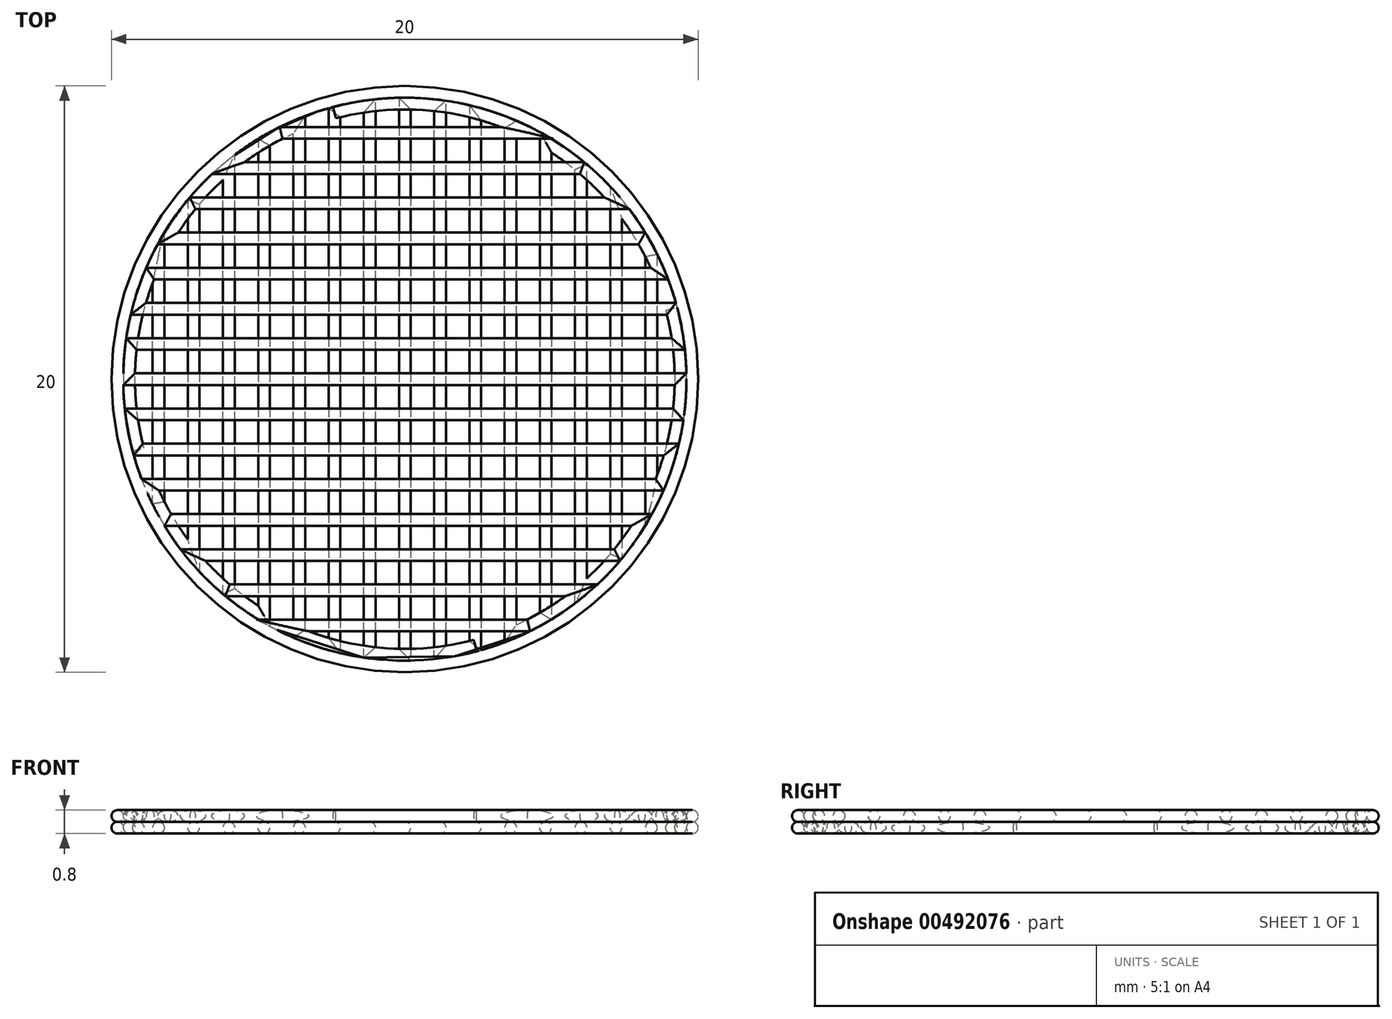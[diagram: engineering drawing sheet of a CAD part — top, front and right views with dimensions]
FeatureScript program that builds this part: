
annotation { "Feature Type Name" : "Feature", "Feature Type Description" : "" }
export const myFeature = defineFeature(function(context is Context, id is Id, definition is map)
    precondition{}
    {
        {
            assignVariable(context, id + "F0", {"name" : "d", "anyValue" : 0.4 * mm});
        }
        {
            var Q0;
            Q0=qCreatedBy(makeId("Top.planeOp"),FACE);
            cPlane(context, id + "F1", {"entities" : qUnion([Q0]), "cplaneType" : CPlaneType.OFFSET, "offset" : getVariable(context, 'd') / 2, "width" : 150 * mm, "height" : 150 * mm});
        }
        {
            var Q0;
            Q0=qCreatedBy(id+"F1.planeOp",FACE);
            var sketch = newSketch(context, id + "F2", { "sketchPlane" : qUnion([Q0])});
            skLineSegment(sketch, "E0.bottom", {"start": v(10, 10) * mm, "end": v(-10, 10) * mm, "construction": true});
            skLineSegment(sketch, "E0.top", {"start": v(10, -10) * mm, "end": v(-10, -10) * mm, "construction": true});
            skLineSegment(sketch, "E0.left", {"start": v(10, 10) * mm, "end": v(10, -10) * mm, "construction": true});
            skLineSegment(sketch, "E0.right", {"start": v(-10, 10) * mm, "end": v(-10, -10) * mm, "construction": true});
            skPoint(sketch, "E0.middle", {"position": v(0, 0) * mm});
            skCircle(sketch, "E1", {"center": v(0, 0) * mm, "radius": 9.8 * mm});
            skCircle(sketch, "E2", {"center": v(0, 0) * mm, "radius": 9.4 * mm, "construction": true});
            skLineSegment(sketch, "E3", {"start": v(10, -10) * mm, "end": v(9.6, -10) * mm, "construction": true});
            skLineSegment(sketch, "E4", {"start": v(9.6, -10) * mm, "end": v(8.4, -10) * mm, "construction": true});
            skLineSegment(sketch, "E5", {"start": v(8.4, -10) * mm, "end": v(7.2, -10) * mm, "construction": true});
            skLineSegment(sketch, "E6", {"start": v(7.2, -10) * mm, "end": v(6, -10) * mm, "construction": true});
            skLineSegment(sketch, "E7", {"start": v(6, -10) * mm, "end": v(4.8, -10) * mm, "construction": true});
            skLineSegment(sketch, "E8", {"start": v(4.8, -10) * mm, "end": v(3.6, -10) * mm, "construction": true});
            skLineSegment(sketch, "E9", {"start": v(3.6, -10) * mm, "end": v(2.4, -10) * mm, "construction": true});
            skLineSegment(sketch, "E10", {"start": v(2.4, -10) * mm, "end": v(1.2, -10) * mm, "construction": true});
            skLineSegment(sketch, "E11", {"start": v(1.2, -10) * mm, "end": v(0, -10) * mm, "construction": true});
            skLineSegment(sketch, "E12", {"start": v(0, -10) * mm, "end": v(-1.2, -10) * mm, "construction": true});
            skLineSegment(sketch, "E13", {"start": v(-1.2, -10) * mm, "end": v(-2.4, -10) * mm, "construction": true});
            skLineSegment(sketch, "E14", {"start": v(-2.4, -10) * mm, "end": v(-3.6, -10) * mm, "construction": true});
            skLineSegment(sketch, "E15", {"start": v(-3.6, -10) * mm, "end": v(-4.8, -10) * mm, "construction": true});
            skLineSegment(sketch, "E16", {"start": v(-4.8, -10) * mm, "end": v(-6, -10) * mm, "construction": true});
            skLineSegment(sketch, "E17", {"start": v(-6, -10) * mm, "end": v(-10, -10) * mm, "construction": true});
            skLineSegment(sketch, "E18", {"start": v(-6, -10) * mm, "end": v(-7.2, -10) * mm, "construction": true});
            skLineSegment(sketch, "E19", {"start": v(-7.2, -10) * mm, "end": v(-8.4, -10) * mm, "construction": true});
            skLineSegment(sketch, "E20", {"start": v(-8.4, -10) * mm, "end": v(-9.6, -10) * mm, "construction": true});
            skLineSegment(sketch, "E21", {"start": v(-9.6, -10) * mm, "end": v(-10, -10) * mm, "construction": true});
            skLineSegment(sketch, "E22", {"start": v(9.6, -10) * mm, "end": v(9.6, 10) * mm, "construction": true});
            skLineSegment(sketch, "E23", {"start": v(9.6, 10) * mm, "end": v(10, 10) * mm, "construction": true});
            skLineSegment(sketch, "E24", {"start": v(-9.6, -10) * mm, "end": v(-9.6, 10) * mm, "construction": true});
            skLineSegment(sketch, "E25", {"start": v(-9.6, 10) * mm, "end": v(-10, 10) * mm, "construction": true});
            skLineSegment(sketch, "E26", {"start": v(7.2, -10) * mm, "end": v(7.2, -6.04) * mm, "construction": true});
            skLineSegment(sketch, "E27", {"start": v(7.2, -6.04) * mm, "end": v(7.2, 6.04) * mm});
            skLineSegment(sketch, "E28", {"start": v(7.2, 6.04) * mm, "end": v(7.2, 10) * mm, "construction": true});
            skLineSegment(sketch, "E29", {"start": v(6, -10) * mm, "end": v(6, -7.24) * mm, "construction": true});
            skLineSegment(sketch, "E30", {"start": v(6, -7.24) * mm, "end": v(6, 7.24) * mm});
            skLineSegment(sketch, "E31", {"start": v(6, 7.24) * mm, "end": v(6, 10) * mm, "construction": true});
            skLineSegment(sketch, "E32", {"start": v(6, 10) * mm, "end": v(7.2, 10) * mm, "construction": true});
            skLineSegment(sketch, "E33", {"start": v(4.8, -10) * mm, "end": v(4.8, -8.08) * mm, "construction": true});
            skLineSegment(sketch, "E34", {"start": v(4.8, -8.08) * mm, "end": v(4.8, 8.08) * mm});
            skLineSegment(sketch, "E35", {"start": v(4.8, 8.08) * mm, "end": v(4.8, 10) * mm, "construction": true});
            skLineSegment(sketch, "E36", {"start": v(4.8, 10) * mm, "end": v(6, 10) * mm, "construction": true});
            skLineSegment(sketch, "E37", {"start": v(3.6, -10) * mm, "end": v(3.6, -8.68) * mm, "construction": true});
            skLineSegment(sketch, "E38", {"start": v(3.6, -8.68) * mm, "end": v(3.6, 8.68) * mm});
            skLineSegment(sketch, "E39", {"start": v(3.6, 8.68) * mm, "end": v(3.6, 10) * mm, "construction": true});
            skLineSegment(sketch, "E40", {"start": v(3.6, 10) * mm, "end": v(4.8, 10) * mm, "construction": true});
            skLineSegment(sketch, "E41", {"start": v(2.4, -10) * mm, "end": v(2.4, -9.09) * mm, "construction": true});
            skLineSegment(sketch, "E42", {"start": v(2.4, -9.09) * mm, "end": v(2.4, 9.09) * mm});
            skLineSegment(sketch, "E43", {"start": v(2.4, 9.09) * mm, "end": v(2.4, 10) * mm, "construction": true});
            skLineSegment(sketch, "E44", {"start": v(2.4, 10) * mm, "end": v(3.6, 10) * mm, "construction": true});
            skLineSegment(sketch, "E45", {"start": v(1.2, -10) * mm, "end": v(1.2, -9.32) * mm, "construction": true});
            skLineSegment(sketch, "E46", {"start": v(1.2, -9.32) * mm, "end": v(1.2, 9.32) * mm});
            skLineSegment(sketch, "E47", {"start": v(1.2, 9.32) * mm, "end": v(1.2, 10) * mm, "construction": true});
            skLineSegment(sketch, "E48", {"start": v(1.2, 10) * mm, "end": v(2.4, 10) * mm, "construction": true});
            skLineSegment(sketch, "E49", {"start": v(0, -10) * mm, "end": v(0, -9.4) * mm, "construction": true});
            skLineSegment(sketch, "E50", {"start": v(0, -9.4) * mm, "end": v(0, 9.4) * mm});
            skLineSegment(sketch, "E51", {"start": v(0, 9.4) * mm, "end": v(0, 10) * mm, "construction": true});
            skLineSegment(sketch, "E52", {"start": v(0, 10) * mm, "end": v(1.2, 10) * mm, "construction": true});
            skLineSegment(sketch, "E53", {"start": v(-1.2, -10) * mm, "end": v(-1.2, -9.32) * mm, "construction": true});
            skLineSegment(sketch, "E54", {"start": v(-1.2, -9.32) * mm, "end": v(-1.2, 9.32) * mm});
            skLineSegment(sketch, "E55", {"start": v(-1.2, 9.32) * mm, "end": v(-1.2, 10) * mm, "construction": true});
            skLineSegment(sketch, "E56", {"start": v(-1.2, 10) * mm, "end": v(0, 10) * mm, "construction": true});
            skLineSegment(sketch, "E57", {"start": v(-2.4, -10) * mm, "end": v(-2.4, -9.09) * mm, "construction": true});
            skLineSegment(sketch, "E58", {"start": v(-2.4, -9.09) * mm, "end": v(-2.4, 9.09) * mm});
            skLineSegment(sketch, "E59", {"start": v(-2.4, 9.09) * mm, "end": v(-2.4, 10) * mm, "construction": true});
            skLineSegment(sketch, "E60", {"start": v(-2.4, 10) * mm, "end": v(-1.2, 10) * mm, "construction": true});
            skLineSegment(sketch, "E61", {"start": v(-3.6, -10) * mm, "end": v(-3.6, -8.68) * mm, "construction": true});
            skLineSegment(sketch, "E62", {"start": v(-3.6, -8.68) * mm, "end": v(-3.6, 8.68) * mm});
            skLineSegment(sketch, "E63", {"start": v(-3.6, 8.68) * mm, "end": v(-3.6, 10) * mm, "construction": true});
            skLineSegment(sketch, "E64", {"start": v(-3.6, 10) * mm, "end": v(-2.4, 10) * mm, "construction": true});
            skLineSegment(sketch, "E65", {"start": v(-4.8, -10) * mm, "end": v(-4.8, -8.08) * mm, "construction": true});
            skLineSegment(sketch, "E66", {"start": v(-4.8, -8.08) * mm, "end": v(-4.8, 8.08) * mm});
            skLineSegment(sketch, "E67", {"start": v(-4.8, 8.08) * mm, "end": v(-4.8, 10) * mm, "construction": true});
            skLineSegment(sketch, "E68", {"start": v(-4.8, 10) * mm, "end": v(-3.6, 10) * mm, "construction": true});
            skLineSegment(sketch, "E69", {"start": v(-6, -10) * mm, "end": v(-6, -7.24) * mm, "construction": true});
            skLineSegment(sketch, "E70", {"start": v(-6, -7.24) * mm, "end": v(-6, 7.24) * mm});
            skLineSegment(sketch, "E71", {"start": v(-6, 7.24) * mm, "end": v(-6, 10) * mm, "construction": true});
            skLineSegment(sketch, "E72", {"start": v(-6, 10) * mm, "end": v(-4.8, 10) * mm, "construction": true});
            skLineSegment(sketch, "E73", {"start": v(-7.2, -10) * mm, "end": v(-7.2, -6.04) * mm, "construction": true});
            skLineSegment(sketch, "E74", {"start": v(-7.2, -6.04) * mm, "end": v(-7.2, 6.04) * mm});
            skLineSegment(sketch, "E75", {"start": v(-7.2, 6.04) * mm, "end": v(-7.2, 10) * mm, "construction": true});
            skLineSegment(sketch, "E76", {"start": v(-7.2, 10) * mm, "end": v(-6, 10) * mm, "construction": true});
            skLineSegment(sketch, "E77", {"start": v(-8.4, -10) * mm, "end": v(-8.4, -4.22) * mm, "construction": true});
            skArc(sketch, "E78", {"start": v(6, 7.24) * mm, "mid": v(5.42, 7.68) * mm, "end": v(4.8, 8.08) * mm});
            skArc(sketch, "E79", {"start": v(3.6, 8.68) * mm, "mid": v(3, 8.9) * mm, "end": v(2.4, 9.09) * mm});
            skArc(sketch, "E80", {"start": v(1.2, 9.32) * mm, "mid": v(0.6, 9.38) * mm, "end": v(0, 9.4) * mm});
            skArc(sketch, "E81", {"start": v(-1.2, 9.32) * mm, "mid": v(-1.8, 9.23) * mm, "end": v(-2.4, 9.09) * mm});
            skArc(sketch, "E82", {"start": v(-3.6, 8.68) * mm, "mid": v(-4.21, 8.4) * mm, "end": v(-4.8, 8.08) * mm});
            skArc(sketch, "E83", {"start": v(-6, 7.24) * mm, "mid": v(-6.63, 6.67) * mm, "end": v(-7.2, 6.04) * mm});
            skArc(sketch, "E84", {"start": v(7.2, -6.04) * mm, "mid": v(6.63, -6.67) * mm, "end": v(6, -7.24) * mm});
            skArc(sketch, "E85", {"start": v(4.8, -8.08) * mm, "mid": v(4.21, -8.4) * mm, "end": v(3.6, -8.68) * mm});
            skArc(sketch, "E86", {"start": v(2.4, -9.09) * mm, "mid": v(1.8, -9.23) * mm, "end": v(1.2, -9.32) * mm});
            skArc(sketch, "E87", {"start": v(0, -9.4) * mm, "mid": v(-0.6, -9.38) * mm, "end": v(-1.2, -9.32) * mm});
            skArc(sketch, "E88", {"start": v(-2.4, -9.09) * mm, "mid": v(-3, -8.9) * mm, "end": v(-3.6, -8.68) * mm});
            skArc(sketch, "E89", {"start": v(-4.8, -8.08) * mm, "mid": v(-5.42, -7.68) * mm, "end": v(-6, -7.24) * mm});
            skArc(sketch, "E90", {"start": v(-7.2, -6.04) * mm, "mid": v(-7.85, -5.17) * mm, "end": v(-8.4, -4.22) * mm});
            skLineSegment(sketch, "E91", {"start": v(8.4, -10) * mm, "end": v(8.4, -5.05) * mm, "construction": true});
            skLineSegment(sketch, "E92", {"start": v(8.4, -5.05) * mm, "end": v(8.4, 4.22) * mm});
            skLineSegment(sketch, "E93", {"start": v(8.4, 4.22) * mm, "end": v(8.4, 10) * mm, "construction": true});
            skLineSegment(sketch, "E94", {"start": v(8.4, 10) * mm, "end": v(9.6, 10) * mm, "construction": true});
            skLineSegment(sketch, "E95", {"start": v(7.2, 10) * mm, "end": v(8.4, 10) * mm, "construction": true});
            skLineSegment(sketch, "E96", {"start": v(-8.4, -4.22) * mm, "end": v(-8.4, 5.05) * mm});
            skLineSegment(sketch, "E97", {"start": v(-8.4, 5.05) * mm, "end": v(-8.4, 10) * mm, "construction": true});
            skLineSegment(sketch, "E98", {"start": v(-8.4, 10) * mm, "end": v(-7.2, 10) * mm, "construction": true});
            skLineSegment(sketch, "E99", {"start": v(-8.4, 10) * mm, "end": v(-9.6, 10) * mm, "construction": true});
            skArc(sketch, "E100", {"start": v(8.4, 4.22) * mm, "mid": v(7.85, 5.17) * mm, "end": v(7.2, 6.04) * mm});
            skLineSegment(sketch, "E101", {"start": v(-8.4, -4.22) * mm, "end": v(-8.4, 4.22) * mm});
            skLineSegment(sketch, "E102", {"start": v(8.4, -4.22) * mm, "end": v(8.4, 4.22) * mm});
            skPoint(sketch, "E103", {"position": v(9.09, 10) * mm});
            skPoint(sketch, "E104", {"position": v(9.09, 2.4) * mm});
            skArc(sketch, "E105", {"start": v(8.4, -4.22) * mm, "mid": v(9.35, -0.97) * mm, "end": v(9.09, 2.4) * mm});
            skPoint(sketch, "E106", {"position": v(-9.09, -10) * mm});
            skPoint(sketch, "E107", {"position": v(-9.09, -2.4) * mm});
            skArc(sketch, "E108", {"start": v(-8.4, 4.22) * mm, "mid": v(-9.35, 0.97) * mm, "end": v(-9.09, -2.4) * mm});
            skSolve(sketch);
        }
        {
            var Q0;
            Q0=sQuery(id+"F2.wireOp",EDGE,"E105");
            var Q1;
            Q1=sQuery(id+"F2.wireOp",VERTEX,"E104");
            cPlane(context, id + "F3", {"entities" : qUnion([Q0, Q1]), "cplaneType" : CPlaneType.CURVE_POINT, "offset" : 25 * mm, "width" : 150 * mm, "height" : 150 * mm});
        }
        {
            var Q0;
            Q0=qCreatedBy(id+"F3.planeOp",FACE);
            var sketch = newSketch(context, id + "F4", { "sketchPlane" : qUnion([Q0])});
            skCircle(sketch, "E109", {"center": v(-9.4, 0.2) * mm, "radius": 0.2 * mm});
            skSolve(sketch);
        }
        {
            var Q0;
            Q0=makeQuery(id+"F4.imprint","IMPRINT",FACE,{"disambiguationData":[TD([[makeQuery(id+"F4.imprint","IMPRINT",EDGE,{"derivedFrom":sQuery(id+"F4.wireOp",EDGE,"E109")}),1.0]])]});
            var Q1;
            Q1=sQuery(id+"F2.wireOp",EDGE,"E105");
            var Q2;
            Q2=sQuery(id+"F2.wireOp",EDGE,"E102");
            var Q3;
            Q3=sQuery(id+"F2.wireOp",EDGE,"E100");
            var Q4;
            Q4=sQuery(id+"F2.wireOp",EDGE,"E27");
            var Q5;
            Q5=sQuery(id+"F2.wireOp",EDGE,"E84");
            var Q6;
            Q6=sQuery(id+"F2.wireOp",EDGE,"E30");
            var Q7;
            Q7=sQuery(id+"F2.wireOp",EDGE,"E78");
            var Q8;
            Q8=sQuery(id+"F2.wireOp",EDGE,"E34");
            var Q9;
            Q9=sQuery(id+"F2.wireOp",EDGE,"E85");
            var Q10;
            Q10=sQuery(id+"F2.wireOp",EDGE,"E38");
            var Q11;
            Q11=sQuery(id+"F2.wireOp",EDGE,"E79");
            var Q12;
            Q12=sQuery(id+"F2.wireOp",EDGE,"E42");
            var Q13;
            Q13=sQuery(id+"F2.wireOp",EDGE,"E86");
            var Q14;
            Q14=sQuery(id+"F2.wireOp",EDGE,"E46");
            var Q15;
            Q15=sQuery(id+"F2.wireOp",EDGE,"E50");
            var Q16;
            Q16=sQuery(id+"F2.wireOp",EDGE,"E80");
            var Q17;
            Q17=sQuery(id+"F2.wireOp",EDGE,"E81");
            var Q18;
            Q18=sQuery(id+"F2.wireOp",EDGE,"E54");
            var Q19;
            Q19=sQuery(id+"F2.wireOp",EDGE,"E58");
            var Q20;
            Q20=sQuery(id+"F2.wireOp",EDGE,"E82");
            var Q21;
            Q21=sQuery(id+"F2.wireOp",EDGE,"E62");
            var Q22;
            Q22=sQuery(id+"F2.wireOp",EDGE,"E66");
            var Q23;
            Q23=sQuery(id+"F2.wireOp",EDGE,"E70");
            var Q24;
            Q24=sQuery(id+"F2.wireOp",EDGE,"E83");
            var Q25;
            Q25=sQuery(id+"F2.wireOp",EDGE,"E74");
            var Q26;
            Q26=sQuery(id+"F2.wireOp",EDGE,"E101");
            var Q27;
            Q27=sQuery(id+"F2.wireOp",EDGE,"E90");
            var Q28;
            Q28=sQuery(id+"F2.wireOp",EDGE,"E89");
            var Q29;
            Q29=sQuery(id+"F2.wireOp",EDGE,"E88");
            var Q30;
            Q30=sQuery(id+"F2.wireOp",EDGE,"E87");
            var Q31;
            Q31=sQuery(id+"F2.wireOp",EDGE,"E108");
            sweep(context, id + "F5", {"profiles" : qUnion([Q0]), "path" : qUnion([Q1, Q2, Q3, Q4, Q5, Q6, Q7, Q8, Q9, Q10, Q11, Q12, Q13, Q14, Q15, Q16, Q17, Q18, Q19, Q20, Q21, Q22, Q23, Q24, Q25, Q26, Q27, Q28, Q29, Q30, Q31])});
        }
        {
            var Q0;
            Q0=qCreatedBy(makeId("Front.planeOp"),FACE);
            var sketch = newSketch(context, id + "F6", { "sketchPlane" : qUnion([Q0])});
            skCircle(sketch, "E110", {"center": v(9.8, 0.2) * mm, "radius": 0.2 * mm});
            skSolve(sketch);
        }
        {
            var Q0;
            Q0=qSketchRegion(id+"F6",true);
            var Q1;
            Q1=sQuery(id+"F2.wireOp",EDGE,"E1");
            sweep(context, id + "F7", {"profiles" : qUnion([Q0]), "path" : qUnion([Q1])});
        }
        {
            var Q0;
            Q0=qCreatedBy(id+"F1.planeOp",FACE);
            cPlane(context, id + "F8", {"entities" : qUnion([Q0]), "cplaneType" : CPlaneType.OFFSET, "offset" : getVariable(context, 'd'), "width" : 150 * mm, "height" : 150 * mm});
        }
        {
            var Q0;
            Q0=qCreatedBy(id+"F8.planeOp",FACE);
            var sketch = newSketch(context, id + "F9", { "sketchPlane" : qUnion([Q0])});
            skLineSegment(sketch, "E111.bottom", {"start": v(-10, 10) * mm, "end": v(-10, -10) * mm, "construction": true});
            skLineSegment(sketch, "E111.top", {"start": v(10, 10) * mm, "end": v(10, -10) * mm, "construction": true});
            skLineSegment(sketch, "E111.left", {"start": v(-10, 10) * mm, "end": v(10, 10) * mm, "construction": true});
            skLineSegment(sketch, "E111.right", {"start": v(-10, -10) * mm, "end": v(10, -10) * mm, "construction": true});
            skPoint(sketch, "E111.middle", {"position": v(0, 0) * mm});
            skCircle(sketch, "E112", {"center": v(0, 0) * mm, "radius": 9.8 * mm});
            skCircle(sketch, "E113", {"center": v(0, 0) * mm, "radius": 9.4 * mm, "construction": true});
            skLineSegment(sketch, "E114", {"start": v(10, 10) * mm, "end": v(10, 9.6) * mm, "construction": true});
            skLineSegment(sketch, "E115", {"start": v(10, 9.6) * mm, "end": v(10, 8.4) * mm, "construction": true});
            skLineSegment(sketch, "E116", {"start": v(10, 8.4) * mm, "end": v(10, 7.2) * mm, "construction": true});
            skLineSegment(sketch, "E117", {"start": v(10, 7.2) * mm, "end": v(10, 6) * mm, "construction": true});
            skLineSegment(sketch, "E118", {"start": v(10, 6) * mm, "end": v(10, 4.8) * mm, "construction": true});
            skLineSegment(sketch, "E119", {"start": v(10, 4.8) * mm, "end": v(10, 3.6) * mm, "construction": true});
            skLineSegment(sketch, "E120", {"start": v(10, 3.6) * mm, "end": v(10, 2.4) * mm, "construction": true});
            skLineSegment(sketch, "E121", {"start": v(10, 2.4) * mm, "end": v(10, 1.2) * mm, "construction": true});
            skLineSegment(sketch, "E122", {"start": v(10, 1.2) * mm, "end": v(10, 0) * mm, "construction": true});
            skLineSegment(sketch, "E123", {"start": v(10, 0) * mm, "end": v(10, -1.2) * mm, "construction": true});
            skLineSegment(sketch, "E124", {"start": v(10, -1.2) * mm, "end": v(10, -2.4) * mm, "construction": true});
            skLineSegment(sketch, "E125", {"start": v(10, -2.4) * mm, "end": v(10, -3.6) * mm, "construction": true});
            skLineSegment(sketch, "E126", {"start": v(10, -3.6) * mm, "end": v(10, -4.8) * mm, "construction": true});
            skLineSegment(sketch, "E127", {"start": v(10, -4.8) * mm, "end": v(10, -6) * mm, "construction": true});
            skLineSegment(sketch, "E128", {"start": v(10, -6) * mm, "end": v(10, -10) * mm, "construction": true});
            skLineSegment(sketch, "E129", {"start": v(10, -6) * mm, "end": v(10, -7.2) * mm, "construction": true});
            skLineSegment(sketch, "E130", {"start": v(10, -7.2) * mm, "end": v(10, -8.4) * mm, "construction": true});
            skLineSegment(sketch, "E131", {"start": v(10, -8.4) * mm, "end": v(10, -9.6) * mm, "construction": true});
            skLineSegment(sketch, "E132", {"start": v(10, -9.6) * mm, "end": v(10, -10) * mm, "construction": true});
            skLineSegment(sketch, "E133", {"start": v(10, 9.6) * mm, "end": v(-10, 9.6) * mm, "construction": true});
            skLineSegment(sketch, "E134", {"start": v(-10, 9.6) * mm, "end": v(-10, 10) * mm, "construction": true});
            skLineSegment(sketch, "E135", {"start": v(10, -9.6) * mm, "end": v(-10, -9.6) * mm, "construction": true});
            skLineSegment(sketch, "E136", {"start": v(-10, -9.6) * mm, "end": v(-10, -10) * mm, "construction": true});
            skLineSegment(sketch, "E137", {"start": v(10, 7.2) * mm, "end": v(6.04, 7.2) * mm, "construction": true});
            skLineSegment(sketch, "E138", {"start": v(6.04, 7.2) * mm, "end": v(-6.04, 7.2) * mm});
            skLineSegment(sketch, "E139", {"start": v(-6.04, 7.2) * mm, "end": v(-10, 7.2) * mm, "construction": true});
            skLineSegment(sketch, "E140", {"start": v(10, 6) * mm, "end": v(7.24, 6) * mm, "construction": true});
            skLineSegment(sketch, "E141", {"start": v(7.24, 6) * mm, "end": v(-7.24, 6) * mm});
            skLineSegment(sketch, "E142", {"start": v(-7.24, 6) * mm, "end": v(-10, 6) * mm, "construction": true});
            skLineSegment(sketch, "E143", {"start": v(-10, 6) * mm, "end": v(-10, 7.2) * mm, "construction": true});
            skLineSegment(sketch, "E144", {"start": v(10, 4.8) * mm, "end": v(8.08, 4.8) * mm, "construction": true});
            skLineSegment(sketch, "E145", {"start": v(8.08, 4.8) * mm, "end": v(-8.08, 4.8) * mm});
            skLineSegment(sketch, "E146", {"start": v(-8.08, 4.8) * mm, "end": v(-10, 4.8) * mm, "construction": true});
            skLineSegment(sketch, "E147", {"start": v(-10, 4.8) * mm, "end": v(-10, 6) * mm, "construction": true});
            skLineSegment(sketch, "E148", {"start": v(10, 3.6) * mm, "end": v(8.68, 3.6) * mm, "construction": true});
            skLineSegment(sketch, "E149", {"start": v(8.68, 3.6) * mm, "end": v(-8.68, 3.6) * mm});
            skLineSegment(sketch, "E150", {"start": v(-8.68, 3.6) * mm, "end": v(-10, 3.6) * mm, "construction": true});
            skLineSegment(sketch, "E151", {"start": v(-10, 3.6) * mm, "end": v(-10, 4.8) * mm, "construction": true});
            skLineSegment(sketch, "E152", {"start": v(10, 2.4) * mm, "end": v(9.09, 2.4) * mm, "construction": true});
            skLineSegment(sketch, "E153", {"start": v(9.09, 2.4) * mm, "end": v(-9.09, 2.4) * mm});
            skLineSegment(sketch, "E154", {"start": v(-9.09, 2.4) * mm, "end": v(-10, 2.4) * mm, "construction": true});
            skLineSegment(sketch, "E155", {"start": v(-10, 2.4) * mm, "end": v(-10, 3.6) * mm, "construction": true});
            skLineSegment(sketch, "E156", {"start": v(10, 1.2) * mm, "end": v(9.32, 1.2) * mm, "construction": true});
            skLineSegment(sketch, "E157", {"start": v(9.32, 1.2) * mm, "end": v(-9.32, 1.2) * mm});
            skLineSegment(sketch, "E158", {"start": v(-9.32, 1.2) * mm, "end": v(-10, 1.2) * mm, "construction": true});
            skLineSegment(sketch, "E159", {"start": v(-10, 1.2) * mm, "end": v(-10, 2.4) * mm, "construction": true});
            skLineSegment(sketch, "E160", {"start": v(10, 0) * mm, "end": v(9.4, 0) * mm, "construction": true});
            skLineSegment(sketch, "E161", {"start": v(9.4, 0) * mm, "end": v(-9.4, 0) * mm});
            skLineSegment(sketch, "E162", {"start": v(-9.4, 0) * mm, "end": v(-10, 0) * mm, "construction": true});
            skLineSegment(sketch, "E163", {"start": v(-10, 0) * mm, "end": v(-10, 1.2) * mm, "construction": true});
            skLineSegment(sketch, "E164", {"start": v(10, -1.2) * mm, "end": v(9.32, -1.2) * mm, "construction": true});
            skLineSegment(sketch, "E165", {"start": v(9.32, -1.2) * mm, "end": v(-9.32, -1.2) * mm});
            skLineSegment(sketch, "E166", {"start": v(-9.32, -1.2) * mm, "end": v(-10, -1.2) * mm, "construction": true});
            skLineSegment(sketch, "E167", {"start": v(-10, -1.2) * mm, "end": v(-10, 0) * mm, "construction": true});
            skLineSegment(sketch, "E168", {"start": v(10, -2.4) * mm, "end": v(9.09, -2.4) * mm, "construction": true});
            skLineSegment(sketch, "E169", {"start": v(9.09, -2.4) * mm, "end": v(-9.09, -2.4) * mm});
            skLineSegment(sketch, "E170", {"start": v(-9.09, -2.4) * mm, "end": v(-10, -2.4) * mm, "construction": true});
            skLineSegment(sketch, "E171", {"start": v(-10, -2.4) * mm, "end": v(-10, -1.2) * mm, "construction": true});
            skLineSegment(sketch, "E172", {"start": v(10, -3.6) * mm, "end": v(8.68, -3.6) * mm, "construction": true});
            skLineSegment(sketch, "E173", {"start": v(8.68, -3.6) * mm, "end": v(-8.68, -3.6) * mm});
            skLineSegment(sketch, "E174", {"start": v(-8.68, -3.6) * mm, "end": v(-10, -3.6) * mm, "construction": true});
            skLineSegment(sketch, "E175", {"start": v(-10, -3.6) * mm, "end": v(-10, -2.4) * mm, "construction": true});
            skLineSegment(sketch, "E176", {"start": v(10, -4.8) * mm, "end": v(8.08, -4.8) * mm, "construction": true});
            skLineSegment(sketch, "E177", {"start": v(8.08, -4.8) * mm, "end": v(-8.08, -4.8) * mm});
            skLineSegment(sketch, "E178", {"start": v(-8.08, -4.8) * mm, "end": v(-10, -4.8) * mm, "construction": true});
            skLineSegment(sketch, "E179", {"start": v(-10, -4.8) * mm, "end": v(-10, -3.6) * mm, "construction": true});
            skLineSegment(sketch, "E180", {"start": v(10, -6) * mm, "end": v(7.24, -6) * mm, "construction": true});
            skLineSegment(sketch, "E181", {"start": v(7.24, -6) * mm, "end": v(-7.24, -6) * mm});
            skLineSegment(sketch, "E182", {"start": v(-7.24, -6) * mm, "end": v(-10, -6) * mm, "construction": true});
            skLineSegment(sketch, "E183", {"start": v(-10, -6) * mm, "end": v(-10, -4.8) * mm, "construction": true});
            skLineSegment(sketch, "E184", {"start": v(10, -7.2) * mm, "end": v(6.04, -7.2) * mm, "construction": true});
            skLineSegment(sketch, "E185", {"start": v(6.04, -7.2) * mm, "end": v(-6.04, -7.2) * mm});
            skLineSegment(sketch, "E186", {"start": v(-6.04, -7.2) * mm, "end": v(-10, -7.2) * mm, "construction": true});
            skLineSegment(sketch, "E187", {"start": v(-10, -7.2) * mm, "end": v(-10, -6) * mm, "construction": true});
            skLineSegment(sketch, "E188", {"start": v(10, -8.4) * mm, "end": v(4.22, -8.4) * mm, "construction": true});
            skArc(sketch, "E189", {"start": v(-7.24, 6) * mm, "mid": v(-7.68, 5.42) * mm, "end": v(-8.08, 4.8) * mm});
            skArc(sketch, "E190", {"start": v(-8.68, 3.6) * mm, "mid": v(-8.9, 3) * mm, "end": v(-9.09, 2.4) * mm});
            skArc(sketch, "E191", {"start": v(-9.32, 1.2) * mm, "mid": v(-9.38, 0.6) * mm, "end": v(-9.4, 0) * mm});
            skArc(sketch, "E192", {"start": v(-9.32, -1.2) * mm, "mid": v(-9.23, -1.8) * mm, "end": v(-9.09, -2.4) * mm});
            skArc(sketch, "E193", {"start": v(-8.68, -3.6) * mm, "mid": v(-8.4, -4.21) * mm, "end": v(-8.08, -4.8) * mm});
            skArc(sketch, "E194", {"start": v(-7.24, -6) * mm, "mid": v(-6.67, -6.63) * mm, "end": v(-6.04, -7.2) * mm});
            skArc(sketch, "E195", {"start": v(6.04, 7.2) * mm, "mid": v(6.67, 6.63) * mm, "end": v(7.24, 6) * mm});
            skArc(sketch, "E196", {"start": v(8.08, 4.8) * mm, "mid": v(8.4, 4.21) * mm, "end": v(8.68, 3.6) * mm});
            skArc(sketch, "E197", {"start": v(9.09, 2.4) * mm, "mid": v(9.23, 1.8) * mm, "end": v(9.32, 1.2) * mm});
            skArc(sketch, "E198", {"start": v(9.4, 0) * mm, "mid": v(9.38, -0.6) * mm, "end": v(9.32, -1.2) * mm});
            skArc(sketch, "E199", {"start": v(9.09, -2.4) * mm, "mid": v(8.9, -3) * mm, "end": v(8.68, -3.6) * mm});
            skArc(sketch, "E200", {"start": v(8.08, -4.8) * mm, "mid": v(7.68, -5.42) * mm, "end": v(7.24, -6) * mm});
            skArc(sketch, "E201", {"start": v(6.04, -7.2) * mm, "mid": v(5.17, -7.85) * mm, "end": v(4.22, -8.4) * mm});
            skLineSegment(sketch, "E202", {"start": v(10, 8.4) * mm, "end": v(5.05, 8.4) * mm, "construction": true});
            skLineSegment(sketch, "E203", {"start": v(5.05, 8.4) * mm, "end": v(-4.22, 8.4) * mm});
            skLineSegment(sketch, "E204", {"start": v(-4.22, 8.4) * mm, "end": v(-10, 8.4) * mm, "construction": true});
            skLineSegment(sketch, "E205", {"start": v(-10, 8.4) * mm, "end": v(-10, 9.6) * mm, "construction": true});
            skLineSegment(sketch, "E206", {"start": v(-10, 7.2) * mm, "end": v(-10, 8.4) * mm, "construction": true});
            skLineSegment(sketch, "E207", {"start": v(4.22, -8.4) * mm, "end": v(-5.05, -8.4) * mm});
            skLineSegment(sketch, "E208", {"start": v(-5.05, -8.4) * mm, "end": v(-10, -8.4) * mm, "construction": true});
            skLineSegment(sketch, "E209", {"start": v(-10, -8.4) * mm, "end": v(-10, -7.2) * mm, "construction": true});
            skLineSegment(sketch, "E210", {"start": v(-10, -8.4) * mm, "end": v(-10, -9.6) * mm, "construction": true});
            skArc(sketch, "E211", {"start": v(-4.22, 8.4) * mm, "mid": v(-5.17, 7.85) * mm, "end": v(-6.04, 7.2) * mm});
            skLineSegment(sketch, "E212", {"start": v(4.22, -8.4) * mm, "end": v(-4.22, -8.4) * mm});
            skLineSegment(sketch, "E213", {"start": v(4.22, 8.4) * mm, "end": v(-4.22, 8.4) * mm});
            skPoint(sketch, "E214", {"position": v(-10, 9.09) * mm});
            skPoint(sketch, "E215", {"position": v(-2.4, 9.09) * mm});
            skArc(sketch, "E216", {"start": v(4.22, 8.4) * mm, "mid": v(0.97, 9.35) * mm, "end": v(-2.4, 9.09) * mm});
            skPoint(sketch, "E217", {"position": v(10, -9.09) * mm});
            skPoint(sketch, "E218", {"position": v(2.4, -9.09) * mm});
            skArc(sketch, "E219", {"start": v(-4.22, -8.4) * mm, "mid": v(-0.97, -9.35) * mm, "end": v(2.4, -9.09) * mm});
            skSolve(sketch);
        }
        {
            var Q0;
            Q0=sQuery(id+"F9.wireOp",VERTEX,"E215");
            var Q1;
            Q1=sQuery(id+"F9.wireOp",EDGE,"E216");
            cPlane(context, id + "F10", {"entities" : qUnion([Q0, Q1]), "cplaneType" : CPlaneType.CURVE_POINT, "offset" : 25 * mm, "width" : 150 * mm, "height" : 150 * mm});
        }
        {
            var Q0;
            Q0=qCreatedBy(id+"F10.planeOp",FACE);
            var sketch = newSketch(context, id + "F11", { "sketchPlane" : qUnion([Q0])});
            skCircle(sketch, "E220", {"center": v(-9.4, 0.6) * mm, "radius": 0.2 * mm});
            skSolve(sketch);
        }
        {
            var Q0;
            Q0=makeQuery(id+"F11.imprint","IMPRINT",FACE,{"disambiguationData":[TD([[makeQuery(id+"F11.imprint","IMPRINT",EDGE,{"derivedFrom":sQuery(id+"F11.wireOp",EDGE,"E220")}),1.0]])]});
            var Q1;
            Q1=sQuery(id+"F9.wireOp",EDGE,"E216");
            var Q2;
            Q2=sQuery(id+"F9.wireOp",EDGE,"E213");
            var Q3;
            Q3=sQuery(id+"F9.wireOp",EDGE,"E211");
            var Q4;
            Q4=sQuery(id+"F9.wireOp",EDGE,"E138");
            var Q5;
            Q5=sQuery(id+"F9.wireOp",EDGE,"E195");
            var Q6;
            Q6=sQuery(id+"F9.wireOp",EDGE,"E141");
            var Q7;
            Q7=sQuery(id+"F9.wireOp",EDGE,"E189");
            var Q8;
            Q8=sQuery(id+"F9.wireOp",EDGE,"E145");
            var Q9;
            Q9=sQuery(id+"F9.wireOp",EDGE,"E149");
            var Q10;
            Q10=sQuery(id+"F9.wireOp",EDGE,"E196");
            var Q11;
            Q11=sQuery(id+"F9.wireOp",EDGE,"E190");
            var Q12;
            Q12=sQuery(id+"F9.wireOp",EDGE,"E153");
            var Q13;
            Q13=sQuery(id+"F9.wireOp",EDGE,"E157");
            var Q14;
            Q14=sQuery(id+"F9.wireOp",EDGE,"E191");
            var Q15;
            Q15=sQuery(id+"F9.wireOp",EDGE,"E161");
            var Q16;
            Q16=sQuery(id+"F9.wireOp",EDGE,"E165");
            var Q17;
            Q17=sQuery(id+"F9.wireOp",EDGE,"E192");
            var Q18;
            Q18=sQuery(id+"F9.wireOp",EDGE,"E169");
            var Q19;
            Q19=sQuery(id+"F9.wireOp",EDGE,"E173");
            var Q20;
            Q20=sQuery(id+"F9.wireOp",EDGE,"E177");
            var Q21;
            Q21=sQuery(id+"F9.wireOp",EDGE,"E193");
            var Q22;
            Q22=sQuery(id+"F9.wireOp",EDGE,"E181");
            var Q23;
            Q23=sQuery(id+"F9.wireOp",EDGE,"E185");
            var Q24;
            Q24=sQuery(id+"F9.wireOp",EDGE,"E194");
            var Q25;
            Q25=sQuery(id+"F9.wireOp",EDGE,"E219");
            var Q26;
            Q26=sQuery(id+"F9.wireOp",EDGE,"E201");
            var Q27;
            Q27=sQuery(id+"F9.wireOp",EDGE,"E200");
            var Q28;
            Q28=sQuery(id+"F9.wireOp",EDGE,"E199");
            var Q29;
            Q29=sQuery(id+"F9.wireOp",EDGE,"E198");
            var Q30;
            Q30=sQuery(id+"F9.wireOp",EDGE,"E197");
            var Q31;
            Q31=sQuery(id+"F9.wireOp",EDGE,"E212");
            sweep(context, id + "F12", {"profiles" : qUnion([Q0]), "path" : qUnion([Q1, Q2, Q3, Q4, Q5, Q6, Q7, Q8, Q9, Q10, Q11, Q12, Q13, Q14, Q15, Q16, Q17, Q18, Q19, Q20, Q21, Q22, Q23, Q24, Q25, Q26, Q27, Q28, Q29, Q30, Q31])});
        }
        {
            var Q0;
            Q0=qCreatedBy(makeId("Right.planeOp"),FACE);
            var sketch = newSketch(context, id + "F13", { "sketchPlane" : qUnion([Q0])});
            skCircle(sketch, "E221", {"center": v(9.8, 0.6) * mm, "radius": 0.2 * mm});
            skSolve(sketch);
        }
        {
            var Q0;
            Q0=makeQuery(id+"F13.imprint","IMPRINT",FACE,{"disambiguationData":[TD([[makeQuery(id+"F13.imprint","IMPRINT",EDGE,{"derivedFrom":sQuery(id+"F13.wireOp",EDGE,"E221")}),1.0]])]});
            var Q1;
            Q1=sQuery(id+"F9.wireOp",EDGE,"E112");
            sweep(context, id + "F14", {"profiles" : qUnion([Q0]), "path" : qUnion([Q1])});
        }
    });
